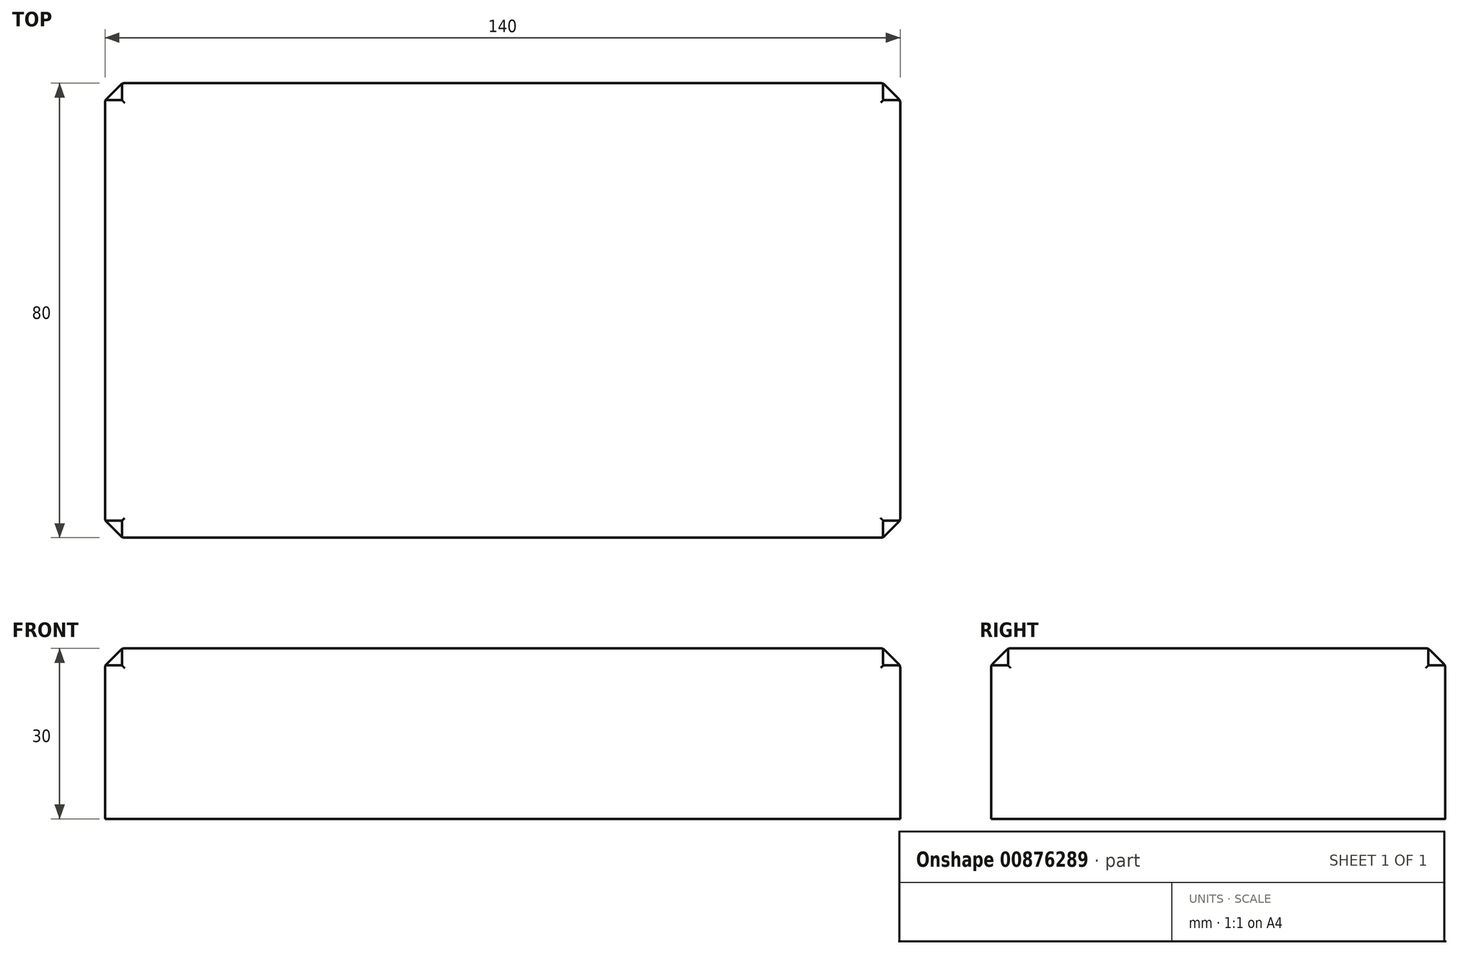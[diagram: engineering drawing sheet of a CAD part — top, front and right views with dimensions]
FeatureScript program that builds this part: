
annotation { "Feature Type Name" : "Feature", "Feature Type Description" : "" }
export const myFeature = defineFeature(function(context is Context, id is Id, definition is map)
    precondition{}
    {
        {
            var Q0;
            Q0=qCreatedBy(makeId("Top.planeOp"),FACE);
            var sketch = newSketch(context, id + "F0", { "sketchPlane" : qUnion([Q0])});
            skLineSegment(sketch, "E0.bottom", {"start": v(70, -40) * mm, "end": v(-70, -40) * mm});
            skLineSegment(sketch, "E0.top", {"start": v(70, 40) * mm, "end": v(-70, 40) * mm});
            skLineSegment(sketch, "E0.left", {"start": v(70, -40) * mm, "end": v(70, 40) * mm});
            skLineSegment(sketch, "E0.right", {"start": v(-70, -40) * mm, "end": v(-70, 40) * mm});
            skPoint(sketch, "E0.middle", {"position": v(0, 0) * mm});
            skSolve(sketch);
        }
        {
            var Q0;
            Q0=qSketchRegion(id+"F0",true);
            extrude(context, id + "F1", {"entities" : qUnion([Q0]), "depth" : 30 * mm, "offsetDistance" : 25 * mm});
        }
        {
            var Q0;
            Q0=makeQuery(id+"F1.opExtrude","CAP_EDGE",EDGE,{"disambiguationData":[OSD([sQuery(id+"F0.wireOp",EDGE,"E0.bottom")])],"isStart":false});
            var Q1;
            Q1=makeQuery(id+"F1.opExtrude","CAP_EDGE",EDGE,{"disambiguationData":[OSD([sQuery(id+"F0.wireOp",EDGE,"E0.right")])],"isStart":false});
            var Q2;
            Q2=makeQuery(id+"F1.opExtrude","CAP_EDGE",EDGE,{"disambiguationData":[OSD([sQuery(id+"F0.wireOp",EDGE,"E0.top")])],"isStart":false});
            var Q3;
            Q3=makeQuery(id+"F1.opExtrude","CAP_EDGE",EDGE,{"disambiguationData":[OSD([sQuery(id+"F0.wireOp",EDGE,"E0.left")])],"isStart":false});
            var Q4;
            Q4=makeQuery(id+"F1.opExtrude","SWEPT_EDGE",EDGE,{"disambiguationData":[OSD([sQuery(id+"F0.wireOp",EDGE,"E0.bottom"),sQuery(id+"F0.wireOp",EDGE,"E0.left")])]});
            var Q5;
            Q5=makeQuery(id+"F1.opExtrude","SWEPT_EDGE",EDGE,{"disambiguationData":[OSD([sQuery(id+"F0.wireOp",EDGE,"E0.bottom"),sQuery(id+"F0.wireOp",EDGE,"E0.right")])]});
            var Q6;
            Q6=makeQuery(id+"F1.opExtrude","SWEPT_EDGE",EDGE,{"disambiguationData":[OSD([sQuery(id+"F0.wireOp",EDGE,"E0.top"),sQuery(id+"F0.wireOp",EDGE,"E0.right")])]});
            var Q7;
            Q7=makeQuery(id+"F1.opExtrude","SWEPT_EDGE",EDGE,{"disambiguationData":[OSD([sQuery(id+"F0.wireOp",EDGE,"E0.top"),sQuery(id+"F0.wireOp",EDGE,"E0.left")])]});
            chamfer(context, id + "F2", {"entities" : qUnion([Q0, Q1, Q2, Q3, Q4, Q5, Q6, Q7]), "width" : 3 * mm, "tangentPropagation" : true});
        }
        {
            var Q0;
            {var subQ0=sQuery(id+"F0.wireOp",EDGE,"E0.left");Q0=makeQuery(id+"F2.opChamfer","BLEND_EDGE",EDGE,{"blendedFrom":[makeQuery(id+"F1.opExtrude","SWEPT_EDGE",EDGE,{"disambiguationData":[OSD([sQuery(id+"F0.wireOp",EDGE,"E0.top"),subQ0])]}),makeQuery(id+"F1.opExtrude","SWEPT_FACE",FACE,{"disambiguationData":[OSD([subQ0])]})],"blendedInto":[makeQuery(id+"F1.opExtrude","SWEPT_FACE",FACE,{"disambiguationData":[OSD([subQ0])]})]});}
            var Q1;
            {var subQ0=sQuery(id+"F0.wireOp",EDGE,"E0.top");Q1=makeQuery(id+"F2.opChamfer","BLEND_EDGE",EDGE,{"blendedFrom":[makeQuery(id+"F1.opExtrude","SWEPT_EDGE",EDGE,{"disambiguationData":[OSD([subQ0,sQuery(id+"F0.wireOp",EDGE,"E0.left")])]}),makeQuery(id+"F1.opExtrude","SWEPT_FACE",FACE,{"disambiguationData":[OSD([subQ0])]})],"blendedInto":[makeQuery(id+"F1.opExtrude","SWEPT_FACE",FACE,{"disambiguationData":[OSD([subQ0])]})]});}
            var Q2;
            {var subQ0=sQuery(id+"F0.wireOp",EDGE,"E0.top");Q2=makeQuery(id+"F2.opChamfer","BLEND_EDGE",EDGE,{"blendedFrom":[makeQuery(id+"F1.opExtrude","CAP_EDGE",EDGE,{"disambiguationData":[OSD([subQ0])],"isStart":false}),makeQuery(id+"F1.opExtrude","SWEPT_FACE",FACE,{"disambiguationData":[OSD([subQ0])]})],"blendedInto":[makeQuery(id+"F1.opExtrude","SWEPT_FACE",FACE,{"disambiguationData":[OSD([subQ0])]})]});}
            var Q3;
            {var subQ0=sQuery(id+"F0.wireOp",EDGE,"E0.top");Q3=makeQuery(id+"F2.opChamfer","BLEND_EDGE",EDGE,{"blendedFrom":[makeQuery(id+"F1.opExtrude","CAP_EDGE",EDGE,{"disambiguationData":[OSD([subQ0])],"isStart":false}),makeQuery(id+"F1.opExtrude","CAP_FACE",FACE,{"disambiguationData":[OSD([sQuery(id+"F0.wireOp",EDGE,"E0.bottom"),subQ0,sQuery(id+"F0.wireOp",EDGE,"E0.left"),sQuery(id+"F0.wireOp",EDGE,"E0.right")])],"isStart":false})],"blendedInto":[makeQuery(id+"F1.opExtrude","CAP_FACE",FACE,{"disambiguationData":[OSD([sQuery(id+"F0.wireOp",EDGE,"E0.bottom"),subQ0,sQuery(id+"F0.wireOp",EDGE,"E0.left"),sQuery(id+"F0.wireOp",EDGE,"E0.right")])],"isStart":false})]});}
            var Q4;
            {var subQ0=sQuery(id+"F0.wireOp",EDGE,"E0.left");Q4=makeQuery(id+"F2.opChamfer","BLEND_EDGE",EDGE,{"blendedFrom":[makeQuery(id+"F1.opExtrude","CAP_EDGE",EDGE,{"disambiguationData":[OSD([subQ0])],"isStart":false}),makeQuery(id+"F1.opExtrude","CAP_FACE",FACE,{"disambiguationData":[OSD([sQuery(id+"F0.wireOp",EDGE,"E0.bottom"),sQuery(id+"F0.wireOp",EDGE,"E0.top"),subQ0,sQuery(id+"F0.wireOp",EDGE,"E0.right")])],"isStart":false})],"blendedInto":[makeQuery(id+"F1.opExtrude","CAP_FACE",FACE,{"disambiguationData":[OSD([sQuery(id+"F0.wireOp",EDGE,"E0.bottom"),sQuery(id+"F0.wireOp",EDGE,"E0.top"),subQ0,sQuery(id+"F0.wireOp",EDGE,"E0.right")])],"isStart":false})]});}
            var Q5;
            {var subQ0=sQuery(id+"F0.wireOp",EDGE,"E0.left");Q5=makeQuery(id+"F2.opChamfer","BLEND_EDGE",EDGE,{"blendedFrom":[makeQuery(id+"F1.opExtrude","CAP_EDGE",EDGE,{"disambiguationData":[OSD([subQ0])],"isStart":false}),makeQuery(id+"F1.opExtrude","SWEPT_FACE",FACE,{"disambiguationData":[OSD([subQ0])]})],"blendedInto":[makeQuery(id+"F1.opExtrude","SWEPT_FACE",FACE,{"disambiguationData":[OSD([subQ0])]})]});}
            var Q6;
            {var subQ0=sQuery(id+"F0.wireOp",EDGE,"E0.top");Q6=makeQuery(id+"F2.opChamfer","BLEND_EDGE",EDGE,{"blendedFrom":[makeQuery(id+"F1.opExtrude","SWEPT_EDGE",EDGE,{"disambiguationData":[OSD([subQ0,sQuery(id+"F0.wireOp",EDGE,"E0.right")])]}),makeQuery(id+"F1.opExtrude","SWEPT_FACE",FACE,{"disambiguationData":[OSD([subQ0])]})],"blendedInto":[makeQuery(id+"F1.opExtrude","SWEPT_FACE",FACE,{"disambiguationData":[OSD([subQ0])]})]});}
            var Q7;
            {var subQ0=sQuery(id+"F0.wireOp",EDGE,"E0.right");Q7=makeQuery(id+"F2.opChamfer","BLEND_EDGE",EDGE,{"blendedFrom":[makeQuery(id+"F1.opExtrude","CAP_EDGE",EDGE,{"disambiguationData":[OSD([subQ0])],"isStart":false}),makeQuery(id+"F1.opExtrude","CAP_FACE",FACE,{"disambiguationData":[OSD([sQuery(id+"F0.wireOp",EDGE,"E0.bottom"),sQuery(id+"F0.wireOp",EDGE,"E0.top"),sQuery(id+"F0.wireOp",EDGE,"E0.left"),subQ0])],"isStart":false})],"blendedInto":[makeQuery(id+"F1.opExtrude","CAP_FACE",FACE,{"disambiguationData":[OSD([sQuery(id+"F0.wireOp",EDGE,"E0.bottom"),sQuery(id+"F0.wireOp",EDGE,"E0.top"),sQuery(id+"F0.wireOp",EDGE,"E0.left"),subQ0])],"isStart":false})]});}
            var Q8;
            {var subQ0=sQuery(id+"F0.wireOp",EDGE,"E0.right");Q8=makeQuery(id+"F2.opChamfer","BLEND_EDGE",EDGE,{"blendedFrom":[makeQuery(id+"F1.opExtrude","CAP_EDGE",EDGE,{"disambiguationData":[OSD([subQ0])],"isStart":false}),makeQuery(id+"F1.opExtrude","SWEPT_FACE",FACE,{"disambiguationData":[OSD([subQ0])]})],"blendedInto":[makeQuery(id+"F1.opExtrude","SWEPT_FACE",FACE,{"disambiguationData":[OSD([subQ0])]})]});}
            var Q9;
            {var subQ0=sQuery(id+"F0.wireOp",EDGE,"E0.right");Q9=makeQuery(id+"F2.opChamfer","BLEND_EDGE",EDGE,{"blendedFrom":[makeQuery(id+"F1.opExtrude","SWEPT_EDGE",EDGE,{"disambiguationData":[OSD([sQuery(id+"F0.wireOp",EDGE,"E0.top"),subQ0])]}),makeQuery(id+"F1.opExtrude","SWEPT_FACE",FACE,{"disambiguationData":[OSD([subQ0])]})],"blendedInto":[makeQuery(id+"F1.opExtrude","SWEPT_FACE",FACE,{"disambiguationData":[OSD([subQ0])]})]});}
            var Q10;
            {var subQ0=sQuery(id+"F0.wireOp",EDGE,"E0.bottom");Q10=makeQuery(id+"F2.opChamfer","BLEND_EDGE",EDGE,{"blendedFrom":[makeQuery(id+"F1.opExtrude","CAP_EDGE",EDGE,{"disambiguationData":[OSD([subQ0])],"isStart":false}),makeQuery(id+"F1.opExtrude","CAP_FACE",FACE,{"disambiguationData":[OSD([subQ0,sQuery(id+"F0.wireOp",EDGE,"E0.top"),sQuery(id+"F0.wireOp",EDGE,"E0.left"),sQuery(id+"F0.wireOp",EDGE,"E0.right")])],"isStart":false})],"blendedInto":[makeQuery(id+"F1.opExtrude","CAP_FACE",FACE,{"disambiguationData":[OSD([subQ0,sQuery(id+"F0.wireOp",EDGE,"E0.top"),sQuery(id+"F0.wireOp",EDGE,"E0.left"),sQuery(id+"F0.wireOp",EDGE,"E0.right")])],"isStart":false})]});}
            var Q11;
            {var subQ0=sQuery(id+"F0.wireOp",EDGE,"E0.left");Q11=makeQuery(id+"F2.opChamfer","BLEND_EDGE",EDGE,{"blendedFrom":[makeQuery(id+"F1.opExtrude","SWEPT_EDGE",EDGE,{"disambiguationData":[OSD([sQuery(id+"F0.wireOp",EDGE,"E0.bottom"),subQ0])]}),makeQuery(id+"F1.opExtrude","SWEPT_FACE",FACE,{"disambiguationData":[OSD([subQ0])]})],"blendedInto":[makeQuery(id+"F1.opExtrude","SWEPT_FACE",FACE,{"disambiguationData":[OSD([subQ0])]})]});}
            var Q12;
            {var subQ0=sQuery(id+"F0.wireOp",EDGE,"E0.bottom");Q12=makeQuery(id+"F2.opChamfer","BLEND_EDGE",EDGE,{"blendedFrom":[makeQuery(id+"F1.opExtrude","SWEPT_EDGE",EDGE,{"disambiguationData":[OSD([subQ0,sQuery(id+"F0.wireOp",EDGE,"E0.left")])]}),makeQuery(id+"F1.opExtrude","SWEPT_FACE",FACE,{"disambiguationData":[OSD([subQ0])]})],"blendedInto":[makeQuery(id+"F1.opExtrude","SWEPT_FACE",FACE,{"disambiguationData":[OSD([subQ0])]})]});}
            var Q13;
            {var subQ0=sQuery(id+"F0.wireOp",EDGE,"E0.bottom");Q13=makeQuery(id+"F2.opChamfer","BLEND_EDGE",EDGE,{"blendedFrom":[makeQuery(id+"F1.opExtrude","CAP_EDGE",EDGE,{"disambiguationData":[OSD([subQ0])],"isStart":false}),makeQuery(id+"F1.opExtrude","SWEPT_FACE",FACE,{"disambiguationData":[OSD([subQ0])]})],"blendedInto":[makeQuery(id+"F1.opExtrude","SWEPT_FACE",FACE,{"disambiguationData":[OSD([subQ0])]})]});}
            var Q14;
            {var subQ0=sQuery(id+"F0.wireOp",EDGE,"E0.right");Q14=makeQuery(id+"F2.opChamfer","BLEND_EDGE",EDGE,{"blendedFrom":[makeQuery(id+"F1.opExtrude","SWEPT_EDGE",EDGE,{"disambiguationData":[OSD([sQuery(id+"F0.wireOp",EDGE,"E0.bottom"),subQ0])]}),makeQuery(id+"F1.opExtrude","SWEPT_FACE",FACE,{"disambiguationData":[OSD([subQ0])]})],"blendedInto":[makeQuery(id+"F1.opExtrude","SWEPT_FACE",FACE,{"disambiguationData":[OSD([subQ0])]})]});}
            var Q15;
            {var subQ0=sQuery(id+"F0.wireOp",EDGE,"E0.bottom");Q15=makeQuery(id+"F2.opChamfer","BLEND_EDGE",EDGE,{"blendedFrom":[makeQuery(id+"F1.opExtrude","SWEPT_EDGE",EDGE,{"disambiguationData":[OSD([subQ0,sQuery(id+"F0.wireOp",EDGE,"E0.right")])]}),makeQuery(id+"F1.opExtrude","SWEPT_FACE",FACE,{"disambiguationData":[OSD([subQ0])]})],"blendedInto":[makeQuery(id+"F1.opExtrude","SWEPT_FACE",FACE,{"disambiguationData":[OSD([subQ0])]})]});}
            fillet(context, id + "F3", {"entities" : qUnion([Q0, Q1, Q2, Q3, Q4, Q5, Q6, Q7, Q8, Q9, Q10, Q11, Q12, Q13, Q14, Q15]), "radius" : 1 * mm, "tangentPropagation" : true, "allowEdgeOverflow" : false});
        }
    });
